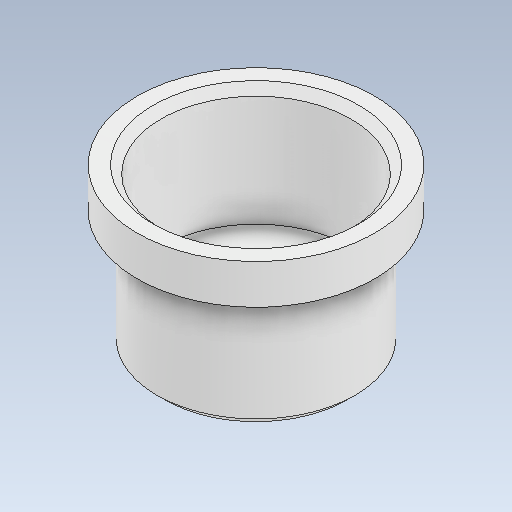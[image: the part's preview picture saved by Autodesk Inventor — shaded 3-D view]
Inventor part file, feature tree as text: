
AUTODESK INVENTOR PART (.ipt)
format: ipt  version: 2020 (Build 240168000, 168)  size: 156,672 bytes
history: native  units: mm
features: extrude x4, other x1, sketch x1, chamfer x1, fillet x1
ambient origin geometry x8: Origin, YZ Plane, XZ Plane, XY Plane, X Axis, Y Axis, Z Axis, Center Point
bodies: Body1 (feature_tree)
feature tree (8):
  other  "Bryła1"
  sketch  "Szkic1"
  extrude  "Wyciągnięcie proste1"  Depth=30.0mm
  extrude  "Wyciągnięcie proste2"  Depth=24.0mm
  extrude  "Wyciągnięcie proste3"  Depth=25.0mm
  chamfer  "Faza1"  Distance=20.0mm
  extrude  "Wyciągnięcie proste4"  Depth=15.0mm TaperAngle=0.0deg
  fillet  "Zaokrąglenie1"  Radius=15.0mm
